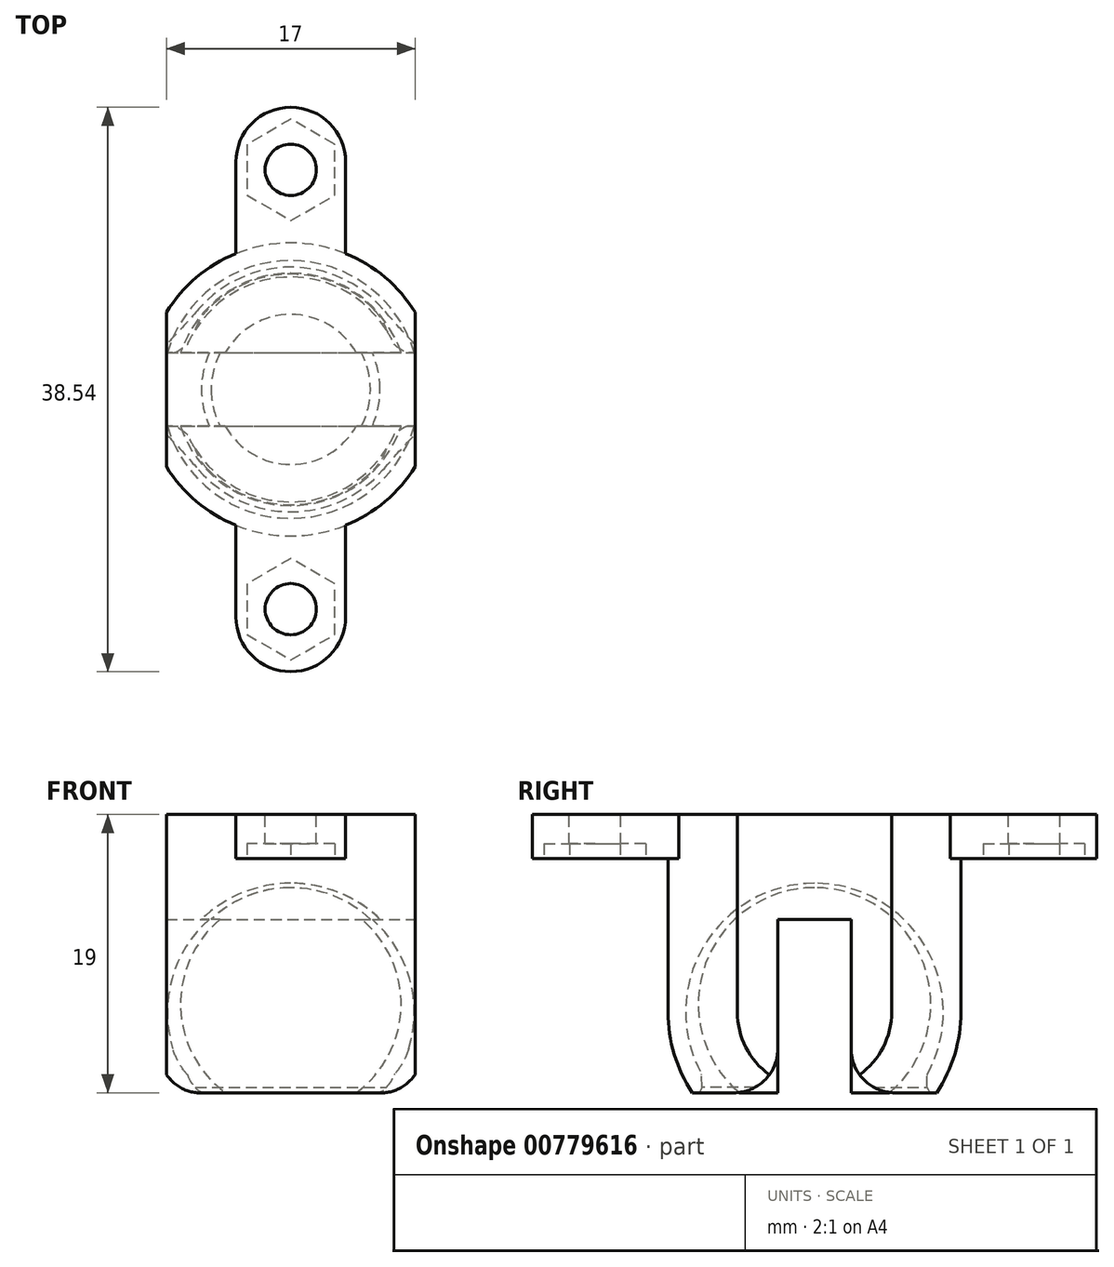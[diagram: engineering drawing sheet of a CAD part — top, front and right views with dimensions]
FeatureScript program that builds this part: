
annotation { "Feature Type Name" : "Feature", "Feature Type Description" : "" }
export const myFeature = defineFeature(function(context is Context, id is Id, definition is map)
    precondition{}
    {
        {
            var Q0;
            Q0=qCreatedBy(makeId("Front.planeOp"),FACE);
            var sketch = newSketch(context, id + "F0", { "sketchPlane" : qUnion([Q0])});
            skArc(sketch, "E0", {"start": v(0, -20.88) * mm, "mid": v(7.94, -12.94) * mm, "end": v(0, -5) * mm});
            skLineSegment(sketch, "E1", {"start": v(0, -20.88) * mm, "end": v(0, -5) * mm});
            skSolve(sketch);
        }
        {
            var Q0;
            Q0 = qSketchRegion(id + "F0", true);
            var Q1;
            Q1=sQuery(id+"F0.wireOp",EDGE,"E1");
            revolve(context, id + "F1", {"surfaceOperationType" : NewSurfaceOperationType.NEW, "entities" : qUnion([Q0]), "axis" : qUnion([Q1]), "revolveType" : RevolveType.FULL});
        }
        {
            var Q0;
            Q0=qCreatedBy(makeId("Front.planeOp"),FACE);
            var sketch = newSketch(context, id + "F2", { "sketchPlane" : qUnion([Q0])});
            skArc(sketch, "E2", {"start": v(-10, -13.5) * mm, "mid": v(-7.07, -20.57) * mm, "end": v(0, -23.5) * mm});
            skLineSegment(sketch, "E3", {"start": v(-10, -13.5) * mm, "end": v(-10, 0) * mm});
            skLineSegment(sketch, "E4", {"start": v(-10, 0) * mm, "end": v(0, 0) * mm});
            skLineSegment(sketch, "E5", {"start": v(0, 0) * mm, "end": v(0, -23.5) * mm});
            skArc(sketch, "E6", {"start": v(0, -4.7) * mm, "mid": v(-8.8, -13.5) * mm, "end": v(0, -22.3) * mm});
            skLineSegment(sketch, "E7", {"start": v(0, -3.5) * mm, "end": v(0, 0) * mm});
            skLineSegment(sketch, "E8", {"start": v(-10, 0) * mm, "end": v(-10, -13.5) * mm});
            skLineSegment(sketch, "E9", {"start": v(0, -4.7) * mm, "end": v(0, 0) * mm});
            skSolve(sketch);
        }
        {
            var Q0;
            {var subQ0=sQuery(id+"F2.wireOp",EDGE,"E5");var subQ1=sQuery(id+"F2.wireOp",EDGE,"E2");var subQ2=makeQuery(id+"F2.imprint","INTERSECT",VERTEX,{"disambiguationData":[OD(0.0)],"derivedFrom":[subQ1,subQ0]});Q0=makeQuery(id+"F2.imprint","IMPRINT",FACE,{"disambiguationData":[TD([[makeQuery(id+"F2.imprint","IMPRINT",EDGE,{"disambiguationData":[TD([[subQ2,-1.0]])],"derivedFrom":subQ1}),1.0]])]});}
            var Q1;
            {var subQ3=sQuery(id+"F2.wireOp",EDGE,"E3");Q1=makeQuery(id+"F2.imprint","IMPRINT",FACE,{"disambiguationData":[TD([[makeQuery(id+"F2.imprint","IMPRINT",EDGE,{"derivedFrom":subQ3}),-1.0]])]});}
            var Q2;
            Q2=sQuery(id+"F2.wireOp",EDGE,"E5");
            revolve(context, id + "F3", {"surfaceOperationType" : NewSurfaceOperationType.NEW, "entities" : qUnion([Q0, Q1]), "axis" : qUnion([Q2]), "revolveType" : RevolveType.FULL});
        }
        {
            var Q0;
            Q0=qCreatedBy(makeId("Top.planeOp"),FACE);
            var sketch = newSketch(context, id + "F4", { "sketchPlane" : qUnion([Q0])});
            skLineSegment(sketch, "E10.bottom", {"start": v(-8.5, 26.95) * mm, "end": v(-18.76, 26.95) * mm});
            skLineSegment(sketch, "E10.top", {"start": v(-8.5, -23.46) * mm, "end": v(-18.76, -23.46) * mm});
            skLineSegment(sketch, "E10.left", {"start": v(-8.5, 26.95) * mm, "end": v(-8.5, -23.46) * mm});
            skLineSegment(sketch, "E10.right", {"start": v(-18.76, 26.95) * mm, "end": v(-18.76, -23.46) * mm});
            skLineSegment(sketch, "E11.bottom", {"start": v(8.5, 34.57) * mm, "end": v(19.05, 34.57) * mm});
            skLineSegment(sketch, "E11.top", {"start": v(8.5, -34.9) * mm, "end": v(19.05, -34.9) * mm});
            skLineSegment(sketch, "E11.left", {"start": v(8.5, 34.57) * mm, "end": v(8.5, -34.9) * mm});
            skLineSegment(sketch, "E11.right", {"start": v(19.05, 34.57) * mm, "end": v(19.05, -34.9) * mm});
            skSolve(sketch);
        }
        {
            var Q0;
            Q0 = qSketchRegion(id + "F4", true);
            extrude(context, id + "F5", {"entities" : qUnion([Q0]), "operationType" : NewBodyOperationType.REMOVE, "oppositeDirection" : true, "depth" : 51.8 * mm, "offsetDistance" : 25 * mm});
        }
        {
            var Q0;
            Q0=qCreatedBy(makeId("Right.planeOp"),FACE);
            var sketch = newSketch(context, id + "F6", { "sketchPlane" : qUnion([Q0])});
            skLineSegment(sketch, "E12.bottom", {"start": v(2.5, -25.16) * mm, "end": v(-2.5, -25.16) * mm});
            skLineSegment(sketch, "E12.top", {"start": v(2.5, -7.16) * mm, "end": v(-2.5, -7.16) * mm});
            skLineSegment(sketch, "E12.left", {"start": v(2.5, -25.16) * mm, "end": v(2.5, -7.16) * mm});
            skLineSegment(sketch, "E12.right", {"start": v(-2.5, -25.16) * mm, "end": v(-2.5, -7.16) * mm});
            skSolve(sketch);
        }
        {
            var Q0;
            Q0 = qSketchRegion(id + "F6", true);
            extrude(context, id + "F7", {"entities" : qUnion([Q0]), "operationType" : NewBodyOperationType.REMOVE, "oppositeDirection" : true, "depth" : 25 * mm, "offsetDistance" : 25 * mm, "symmetric" : true});
        }
        {
            var Q0;
            Q0=qCreatedBy(makeId("Front.planeOp"),FACE);
            var sketch = newSketch(context, id + "F8", { "sketchPlane" : qUnion([Q0])});
            skLineSegment(sketch, "E13.bottom", {"start": v(36.13, -40.51) * mm, "end": v(-27.84, -40.51) * mm});
            skLineSegment(sketch, "E13.top", {"start": v(36.13, -19) * mm, "end": v(-27.84, -19) * mm});
            skLineSegment(sketch, "E13.left", {"start": v(36.13, -40.51) * mm, "end": v(36.13, -19) * mm});
            skLineSegment(sketch, "E13.right", {"start": v(-27.84, -40.51) * mm, "end": v(-27.84, -19) * mm});
            skSolve(sketch);
        }
        {
            var Q0;
            Q0 = qSketchRegion(id + "F8", true);
            extrude(context, id + "F9", {"entities" : qUnion([Q0]), "operationType" : NewBodyOperationType.REMOVE, "oppositeDirection" : true, "depth" : 25 * mm, "offsetDistance" : 25 * mm, "symmetric" : true});
        }
        {
            var Q0;
            Q0=makeQuery(id+"F9.boolean.opBoolean","INTERSECT",EDGE,{"disambiguationData":[OD(1.0)],"derivedFrom":[makeQuery(id+"F3.opRevolve","SWEPT_FACE",FACE,{"disambiguationData":[OSD([sQuery(id+"F2.wireOp",EDGE,"E6")])]}),makeQuery(id+"F9.opExtrude","SWEPT_FACE",FACE,{"disambiguationData":[OSD([sQuery(id+"F8.wireOp",EDGE,"E13.top")])]})]});
            var Q1;
            Q1=makeQuery(id+"F9.boolean.opBoolean","INTERSECT",EDGE,{"disambiguationData":[OD(0.0)],"derivedFrom":[makeQuery(id+"F3.opRevolve","SWEPT_FACE",FACE,{"disambiguationData":[OSD([sQuery(id+"F2.wireOp",EDGE,"E6")])]}),makeQuery(id+"F9.opExtrude","SWEPT_FACE",FACE,{"disambiguationData":[OSD([sQuery(id+"F8.wireOp",EDGE,"E13.top")])]})]});
            chamfer(context, id + "F10", {"entities" : qUnion([Q0, Q1]), "width" : 1 * mm, "tangentPropagation" : true});
        }
        {
            var Q0;
            Q0=qCreatedBy(makeId("Top.planeOp"),FACE);
            var sketch = newSketch(context, id + "F11", { "sketchPlane" : qUnion([Q0])});
            skLineSegment(sketch, "E14.bottom", {"start": v(3.75, 15.52) * mm, "end": v(-3.75, 15.52) * mm});
            skLineSegment(sketch, "E14.top", {"start": v(3.75, 9.27) * mm, "end": v(-3.75, 9.27) * mm});
            skLineSegment(sketch, "E14.left", {"start": v(3.75, 15.52) * mm, "end": v(3.75, 9.27) * mm});
            skLineSegment(sketch, "E14.right", {"start": v(-3.75, 15.52) * mm, "end": v(-3.75, 9.27) * mm});
            skPoint(sketch, "E14.middle", {"position": v(0, 12.4) * mm});
            skLineSegment(sketch, "E15.bottom", {"start": v(-3.75, -9.27) * mm, "end": v(3.75, -9.27) * mm});
            skLineSegment(sketch, "E15.top", {"start": v(-3.75, -15.52) * mm, "end": v(3.75, -15.52) * mm});
            skLineSegment(sketch, "E15.left", {"start": v(-3.75, -9.27) * mm, "end": v(-3.75, -15.52) * mm});
            skLineSegment(sketch, "E15.right", {"start": v(3.75, -9.27) * mm, "end": v(3.75, -15.52) * mm});
            skPoint(sketch, "E15.middle", {"position": v(0, -12.4) * mm});
            skArc(sketch, "E16", {"start": v(3.75, 15.52) * mm, "mid": v(0, 19.27) * mm, "end": v(-3.75, 15.52) * mm});
            skArc(sketch, "E17", {"start": v(-3.75, -15.52) * mm, "mid": v(0, -19.27) * mm, "end": v(3.75, -15.52) * mm});
            skCircle(sketch, "E18", {"center": v(0, 15) * mm, "radius": 1.75 * mm});
            skCircle(sketch, "E19", {"center": v(0, -15) * mm, "radius": 1.75 * mm});
            skArc(sketch, "E20.0", {"start": v(8.5, 5.27) * mm, "mid": v(0, 10) * mm, "end": v(-8.5, 5.27) * mm, "construction": true});
            skArc(sketch, "E21.0", {"start": v(-8.5, -5.27) * mm, "mid": v(0, -10) * mm, "end": v(8.5, -5.27) * mm, "construction": true});
            skSolve(sketch);
        }
        {
            var Q0;
            Q0 = qSketchRegion(id + "F11", true);
            extrude(context, id + "F12", {"entities" : qUnion([Q0]), "operationType" : NewBodyOperationType.ADD, "oppositeDirection" : true, "depth" : 3 * mm, "offsetDistance" : 25 * mm});
        }
        {
            var Q0;
            Q0=makeQuery(id+"F12.opExtrude","CAP_FACE",FACE,{"disambiguationData":[OSD([sQuery(id+"F11.wireOp",EDGE,"E14.top"),sQuery(id+"F11.wireOp",EDGE,"E14.left"),sQuery(id+"F11.wireOp",EDGE,"E14.right"),sQuery(id+"F11.wireOp",EDGE,"E16"),sQuery(id+"F11.wireOp",EDGE,"E18")])],"isStart":false});
            var sketch = newSketch(context, id + "F13", { "sketchPlane" : qUnion([Q0])});
            skCircle(sketch, "E22.cCircle", {"center": v(0, -15) * mm, "radius": 3 * mm, "construction": true});
            skLineSegment(sketch, "E22.0", {"start": v(0, -18.46) * mm, "end": v(-3, -16.73) * mm});
            skLineSegment(sketch, "E22.1", {"start": v(-3, -16.73) * mm, "end": v(-3, -13.27) * mm});
            skLineSegment(sketch, "E22.2", {"start": v(-3, -13.27) * mm, "end": v(0, -11.54) * mm});
            skLineSegment(sketch, "E22.3", {"start": v(0, -11.54) * mm, "end": v(3, -13.27) * mm});
            skLineSegment(sketch, "E22.4", {"start": v(3, -13.27) * mm, "end": v(3, -16.73) * mm});
            skLineSegment(sketch, "E22.5", {"start": v(3, -16.73) * mm, "end": v(0, -18.46) * mm});
            skPoint(sketch, "E22.0.midPoint", {"position": v(-1.5, -17.6) * mm});
            skCircle(sketch, "E23.cCircle", {"center": v(0, 15) * mm, "radius": 3 * mm, "construction": true});
            skLineSegment(sketch, "E23.0", {"start": v(0, 11.54) * mm, "end": v(-3, 13.27) * mm});
            skLineSegment(sketch, "E23.1", {"start": v(-3, 13.27) * mm, "end": v(-3, 16.73) * mm});
            skLineSegment(sketch, "E23.2", {"start": v(-3, 16.73) * mm, "end": v(0, 18.46) * mm});
            skLineSegment(sketch, "E23.3", {"start": v(0, 18.46) * mm, "end": v(3, 16.73) * mm});
            skLineSegment(sketch, "E23.4", {"start": v(3, 16.73) * mm, "end": v(3, 13.27) * mm});
            skLineSegment(sketch, "E23.5", {"start": v(3, 13.27) * mm, "end": v(0, 11.54) * mm});
            skPoint(sketch, "E23.0.midPoint", {"position": v(-1.5, 12.4) * mm});
            skCircle(sketch, "E24.0", {"center": v(0, 15) * mm, "radius": 1.75 * mm, "construction": true});
            skSolve(sketch);
        }
        {
            var Q0;
            Q0 = qSketchRegion(id + "F13", true);
            extrude(context, id + "F14", {"entities" : qUnion([Q0]), "operationType" : NewBodyOperationType.REMOVE, "oppositeDirection" : true, "depth" : 1 * mm, "offsetDistance" : 25 * mm});
        }
        {
            var Q0;
            {var subQ0=makeQuery(id+"F3.opRevolve","SWEPT_FACE",FACE,{"disambiguationData":[OSD([sQuery(id+"F2.wireOp",EDGE,"E6")])]});Q0=makeQuery(id+"F10.opChamfer","BLEND_EDGE",EDGE,{"blendedFrom":[makeQuery(id+"F9.boolean.opBoolean","INTERSECT",EDGE,{"disambiguationData":[OD(0.0)],"derivedFrom":[subQ0,makeQuery(id+"F9.opExtrude","SWEPT_FACE",FACE,{"disambiguationData":[OSD([sQuery(id+"F8.wireOp",EDGE,"E13.top")])]})]}),subQ0],"blendedInto":[subQ0]});}
            var Q1;
            {var subQ0=makeQuery(id+"F3.opRevolve","SWEPT_FACE",FACE,{"disambiguationData":[OSD([sQuery(id+"F2.wireOp",EDGE,"E6")])]});Q1=makeQuery(id+"F10.opChamfer","BLEND_EDGE",EDGE,{"blendedFrom":[makeQuery(id+"F9.boolean.opBoolean","INTERSECT",EDGE,{"disambiguationData":[OD(1.0)],"derivedFrom":[subQ0,makeQuery(id+"F9.opExtrude","SWEPT_FACE",FACE,{"disambiguationData":[OSD([sQuery(id+"F8.wireOp",EDGE,"E13.top")])]})]}),subQ0],"blendedInto":[subQ0]});}
            chamfer(context, id + "F15", {"entities" : qUnion([Q0, Q1]), "width" : 0.5 * mm, "tangentPropagation" : true});
        }
        {
            var Q0;
            Q0=makeQuery(id+"F9.boolean.opBoolean","INTERSECT",EDGE,{"disambiguationData":[OD(1.0)],"derivedFrom":[makeQuery(id+"F7.boolean.opBoolean","COPY",FACE,{"derivedFrom":makeQuery(id+"F7.opExtrude","SWEPT_FACE",FACE,{"disambiguationData":[OSD([sQuery(id+"F6.wireOp",EDGE,"E12.right")])]})}),makeQuery(id+"F9.opExtrude","SWEPT_FACE",FACE,{"disambiguationData":[OSD([sQuery(id+"F8.wireOp",EDGE,"E13.top")])]})]});
            var Q1;
            Q1=makeQuery(id+"F9.boolean.opBoolean","INTERSECT",EDGE,{"disambiguationData":[OD(1.0)],"derivedFrom":[makeQuery(id+"F7.boolean.opBoolean","COPY",FACE,{"derivedFrom":makeQuery(id+"F7.opExtrude","SWEPT_FACE",FACE,{"disambiguationData":[OSD([sQuery(id+"F6.wireOp",EDGE,"E12.left")])]})}),makeQuery(id+"F9.opExtrude","SWEPT_FACE",FACE,{"disambiguationData":[OSD([sQuery(id+"F8.wireOp",EDGE,"E13.top")])]})]});
            var Q2;
            Q2=makeQuery(id+"F9.boolean.opBoolean","INTERSECT",EDGE,{"disambiguationData":[OD(0.0)],"derivedFrom":[makeQuery(id+"F7.boolean.opBoolean","COPY",FACE,{"derivedFrom":makeQuery(id+"F7.opExtrude","SWEPT_FACE",FACE,{"disambiguationData":[OSD([sQuery(id+"F6.wireOp",EDGE,"E12.left")])]})}),makeQuery(id+"F9.opExtrude","SWEPT_FACE",FACE,{"disambiguationData":[OSD([sQuery(id+"F8.wireOp",EDGE,"E13.top")])]})]});
            var Q3;
            Q3=makeQuery(id+"F9.boolean.opBoolean","INTERSECT",EDGE,{"disambiguationData":[OD(0.0)],"derivedFrom":[makeQuery(id+"F7.boolean.opBoolean","COPY",FACE,{"derivedFrom":makeQuery(id+"F7.opExtrude","SWEPT_FACE",FACE,{"disambiguationData":[OSD([sQuery(id+"F6.wireOp",EDGE,"E12.right")])]})}),makeQuery(id+"F9.opExtrude","SWEPT_FACE",FACE,{"disambiguationData":[OSD([sQuery(id+"F8.wireOp",EDGE,"E13.top")])]})]});
            fillet(context, id + "F16", {"entities" : qUnion([Q0, Q1, Q2, Q3]), "tangentPropagation" : true, "radius" : 3 * mm, "defaultsChanged" : true, "vertexSettings" : [], "allowEdgeOverflow" : false});
        }
        {
            var Q0;
            {var subQ0=makeQuery(id+"F3.opRevolve","SWEPT_FACE",FACE,{"disambiguationData":[OSD([sQuery(id+"F2.wireOp",EDGE,"E6")])]});var subQ1=subQ0;Q0=makeQuery(id+"F15.opChamfer","BLEND_EDGE",EDGE,{"blendedFrom":[makeQuery(id+"F10.opChamfer","BLEND_EDGE",EDGE,{"blendedFrom":[makeQuery(id+"F9.boolean.opBoolean","INTERSECT",EDGE,{"disambiguationData":[OD(0.0)],"derivedFrom":[subQ0,makeQuery(id+"F9.opExtrude","SWEPT_FACE",FACE,{"disambiguationData":[OSD([sQuery(id+"F8.wireOp",EDGE,"E13.top")])]})]}),subQ1],"blendedInto":[subQ1]}),subQ1],"blendedInto":[subQ1]});}
            var Q1;
            {var subQ0=makeQuery(id+"F3.opRevolve","SWEPT_FACE",FACE,{"disambiguationData":[OSD([sQuery(id+"F2.wireOp",EDGE,"E6")])]});var subQ1=subQ0;Q1=makeQuery(id+"F15.opChamfer","BLEND_EDGE",EDGE,{"blendedFrom":[makeQuery(id+"F10.opChamfer","BLEND_EDGE",EDGE,{"blendedFrom":[makeQuery(id+"F9.boolean.opBoolean","INTERSECT",EDGE,{"disambiguationData":[OD(1.0)],"derivedFrom":[subQ0,makeQuery(id+"F9.opExtrude","SWEPT_FACE",FACE,{"disambiguationData":[OSD([sQuery(id+"F8.wireOp",EDGE,"E13.top")])]})]}),subQ1],"blendedInto":[subQ1]}),subQ1],"blendedInto":[subQ1]});}
            fillet(context, id + "F17", {"entities" : qUnion([Q0, Q1]), "tangentPropagation" : true, "radius" : 0.1 * mm, "defaultsChanged" : true, "vertexSettings" : [], "allowEdgeOverflow" : false});
        }
    });
